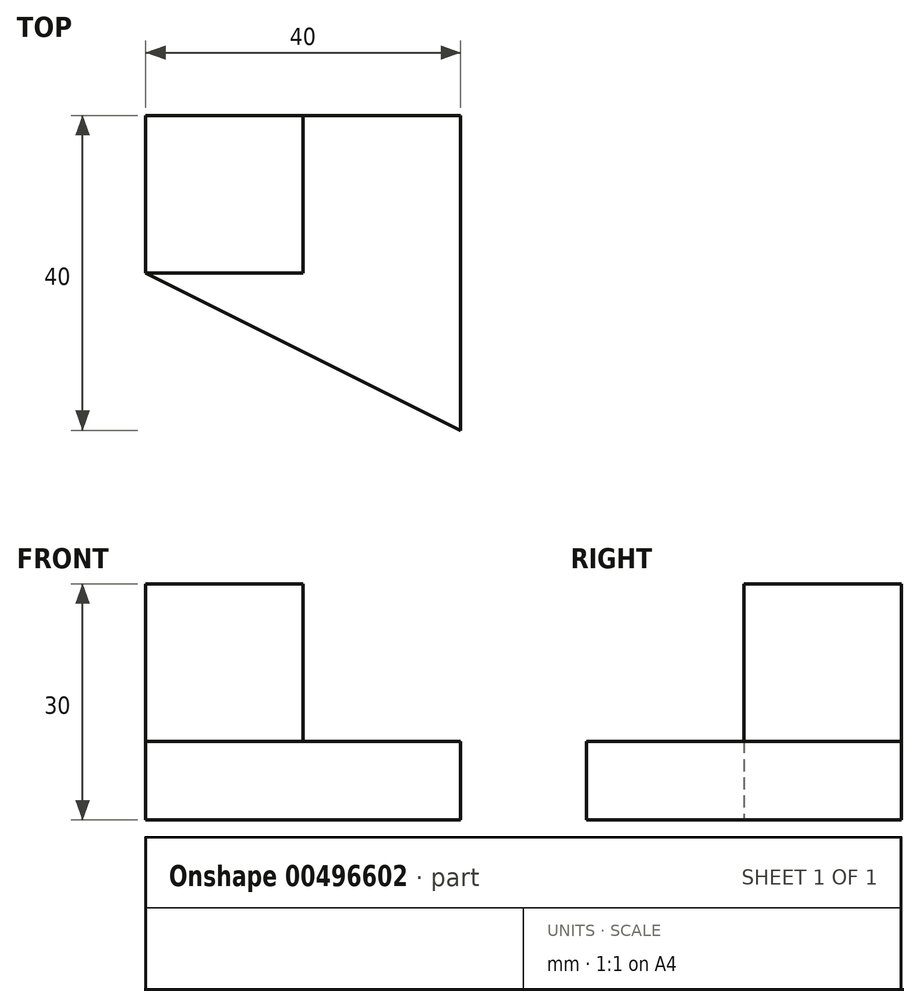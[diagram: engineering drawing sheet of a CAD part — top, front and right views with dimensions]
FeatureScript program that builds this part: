
annotation { "Feature Type Name" : "Feature", "Feature Type Description" : "" }
export const myFeature = defineFeature(function(context is Context, id is Id, definition is map)
    precondition{}
    {
        {
            var Q0;
            Q0=qCreatedBy(makeId("Top.planeOp"),FACE);
            var sketch = newSketch(context, id + "F0", { "sketchPlane" : qUnion([Q0])});
            skLineSegment(sketch, "E0", {"start": v(0, 0) * mm, "end": v(0, 20) * mm});
            skLineSegment(sketch, "E1", {"start": v(0, 20) * mm, "end": v(40, 20) * mm});
            skLineSegment(sketch, "E2", {"start": v(40, 20) * mm, "end": v(40, -20) * mm});
            skLineSegment(sketch, "E3", {"start": v(0, 0) * mm, "end": v(40, -20) * mm});
            skSolve(sketch);
        }
        {
            var Q0;
            Q0 = qSketchRegion(id + "F0", true);
            extrude(context, id + "F1", {"entities" : qUnion([Q0]), "depth" : 10 * mm});
        }
        {
            var Q0;
            Q0=makeQuery(id+"F1.opExtrude","CAP_FACE",FACE,{"disambiguationData":[OSD([sQuery(id+"F0.wireOp",EDGE,"E0"),sQuery(id+"F0.wireOp",EDGE,"E1"),sQuery(id+"F0.wireOp",EDGE,"E2"),sQuery(id+"F0.wireOp",EDGE,"E3")])],"isStart":false});
            var sketch = newSketch(context, id + "F2", { "sketchPlane" : qUnion([Q0])});
            skLineSegment(sketch, "E4", {"start": v(0, 0) * mm, "end": v(20, 0) * mm});
            skLineSegment(sketch, "E5", {"start": v(20, 0) * mm, "end": v(20, 20) * mm});
            skLineSegment(sketch, "E6", {"start": v(20, 20) * mm, "end": v(0, 20) * mm});
            skLineSegment(sketch, "E7", {"start": v(0, 20) * mm, "end": v(0, 0) * mm});
            skSolve(sketch);
        }
        {
            var Q0;
            Q0=makeQuery(id+"F2.imprint","IMPRINT",FACE,{"disambiguationData":[TD([[makeQuery(id+"F2.imprint","IMPRINT",EDGE,{"derivedFrom":sQuery(id+"F2.wireOp",EDGE,"E4")}),1.0]])]});
            extrude(context, id + "F3", {"entities" : qUnion([Q0]), "operationType" : NewBodyOperationType.ADD, "depth" : 20 * mm});
        }
    });
